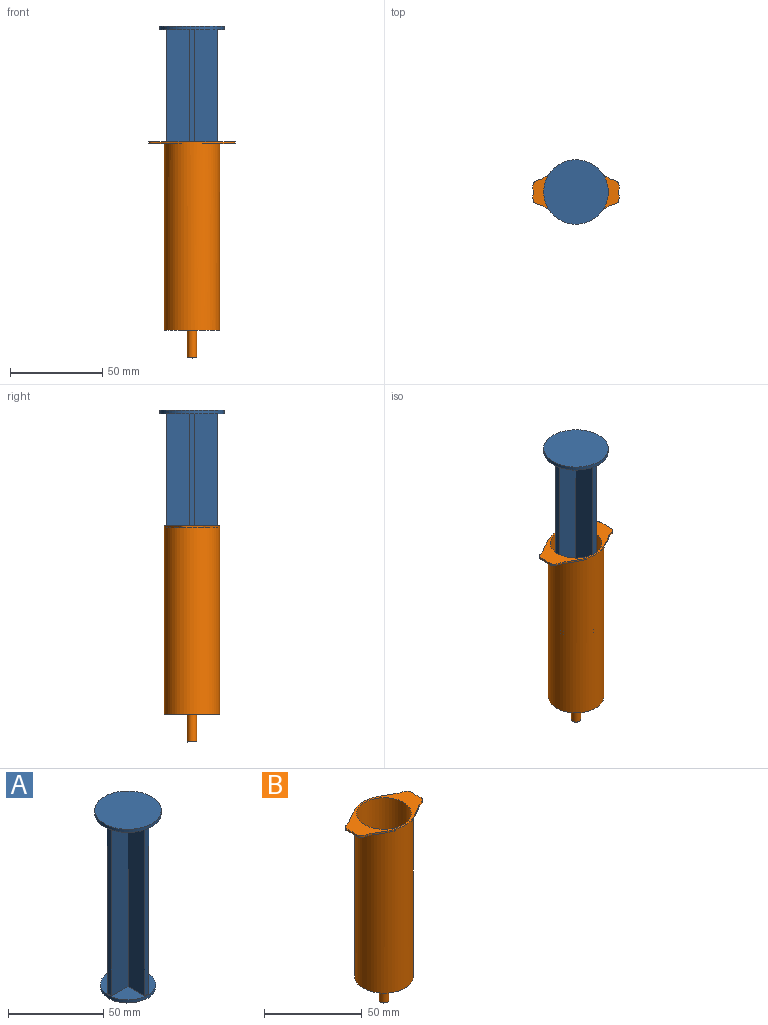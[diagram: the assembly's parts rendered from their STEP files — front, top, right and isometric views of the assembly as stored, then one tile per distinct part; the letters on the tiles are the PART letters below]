
ASSEMBLY  parts=2 mates=1
PART A: 18 faces, bbox 35x35x114 mm
  f0: plane 35x35mm, normal (0,0,-1), area 792.7mm2, adj f1,f3,f4,f5,f6,f7,f8,f9
  f1: cylinder r=17.5mm len=35mm, axis (0,0,-1), area 219.9mm2, adj f0,f2
  f2: plane 35x35mm, normal (0,0,1), area 962.1mm2, adj f1
  f3: plane 110x12.4mm, normal (1,0,0), area 1363.5mm2, adj f0,f4,f14,f15
  f4: plane 110x3.21mm, normal (0,1,0), area 353.1mm2, adj f0,f3,f5,f15
  f5: plane 110x12.4mm, normal (-1,0,0), area 1363.5mm2, adj f0,f4,f6,f15
  f6: plane 110x12.4mm, normal (0,1,0), area 1363.5mm2, adj f0,f5,f7,f15
  f7: plane 110x3.21mm, normal (-1,0,0), area 353.1mm2, adj f0,f6,f8,f15
  f8: plane 110x12.4mm, normal (0,-1,0), area 1363.5mm2, adj f0,f7,f9,f15
  f9: plane 110x12.4mm, normal (-1,0,0), area 1363.5mm2, adj f0,f8,f10,f15
  f10: plane 110x3.21mm, normal (0,-1,0), area 353.1mm2, adj f0,f9,f11,f15
  f11: plane 110x12.4mm, normal (1,0,0), area 1363.5mm2, adj f0,f10,f12,f15
  f12: plane 110x12.4mm, normal (0,-1,0), area 1363.5mm2, adj f0,f11,f13,f15
  f13: plane 110x3.21mm, normal (1,0,0), area 353.1mm2, adj f0,f12,f14,f15
  f14: plane 110x12.4mm, normal (0,1,0), area 1363.5mm2, adj f0,f3,f13,f15
  f15: plane 29x29mm, normal (0,0,1), area 491.1mm2, adj f3,f4,f5,f6,f7,f8,f9,f10
  f16: cylinder r=14.5mm len=29mm, axis (0,0,1), area 182.2mm2, adj f15,f17
  f17: plane 29x29mm, normal (0,0,-1), area 660.5mm2, adj f16
PART B: 18 faces, bbox 47x30x117 mm
  f0: cylinder r=15mm len=102mm, axis (0,0,1), area 9542.5mm2, adj f1,f2,f8,f11,f12,f14,f15,f17
  f1: plane 30x30mm, normal (0,0,-1), area 687.2mm2, adj f0,f3
  f2: plane 47.03x30mm, normal (0,0,1), area 390.6mm2, adj f0,f5,f8,f9,f10,f11,f13,f14
  f3: cylinder r=2.5mm len=15mm, axis (0,0,1), area 235.6mm2, adj f1,f4
  f4: plane 5x5mm, normal (0,0,-1), area 12.6mm2, adj f3,f7
  f5: cylinder r=14mm len=101mm, axis (0,0,1), area 8884.4mm2, adj f2,f6
  f6: plane 28x28mm, normal (0,0,1), area 608.7mm2, adj f5,f7
  f7: cylinder r=1.5mm len=16mm, axis (0,0,1), area 150.8mm2, adj f4,f6
  f8: extruded ~10.98x5.62mm, area 12.4mm2, adj f0,f2,f9,f12
  f9: extruded ~8.24x6.62mm, area 12.3mm2, adj f2,f8,f10,f12
  f10: extruded ~8.24x6.62mm, area 12.3mm2, adj f2,f9,f11,f12
  f11: extruded ~10.98x5.62mm, area 12.4mm2, adj f0,f2,f10,f12
  f12: plane 27.92x17.88mm, normal (0,0,-1), area 149.7mm2, adj f0,f8,f9,f10,f11
  f13: extruded ~8.24x6.62mm, area 12.3mm2, adj f2,f14,f16,f17
  f14: extruded ~10.98x5.62mm, area 12.4mm2, adj f0,f2,f13,f17
  f15: extruded ~10.98x5.62mm, area 12.4mm2, adj f0,f2,f16,f17
  f16: extruded ~8.24x6.62mm, area 12.3mm2, adj f2,f13,f15,f17
  f17: plane 27.92x17.88mm, normal (0,0,-1), area 149.7mm2, adj f0,f13,f14,f15,f16
PLACE A t=(-43.08,28.19,145.17)mm
PLACE B t=(-43.08,28.19,-15.64)mm
MATE slider B.f0 <-> A.f16  axis (0,0,1) through (-43.08,28.19,84.36)mm
